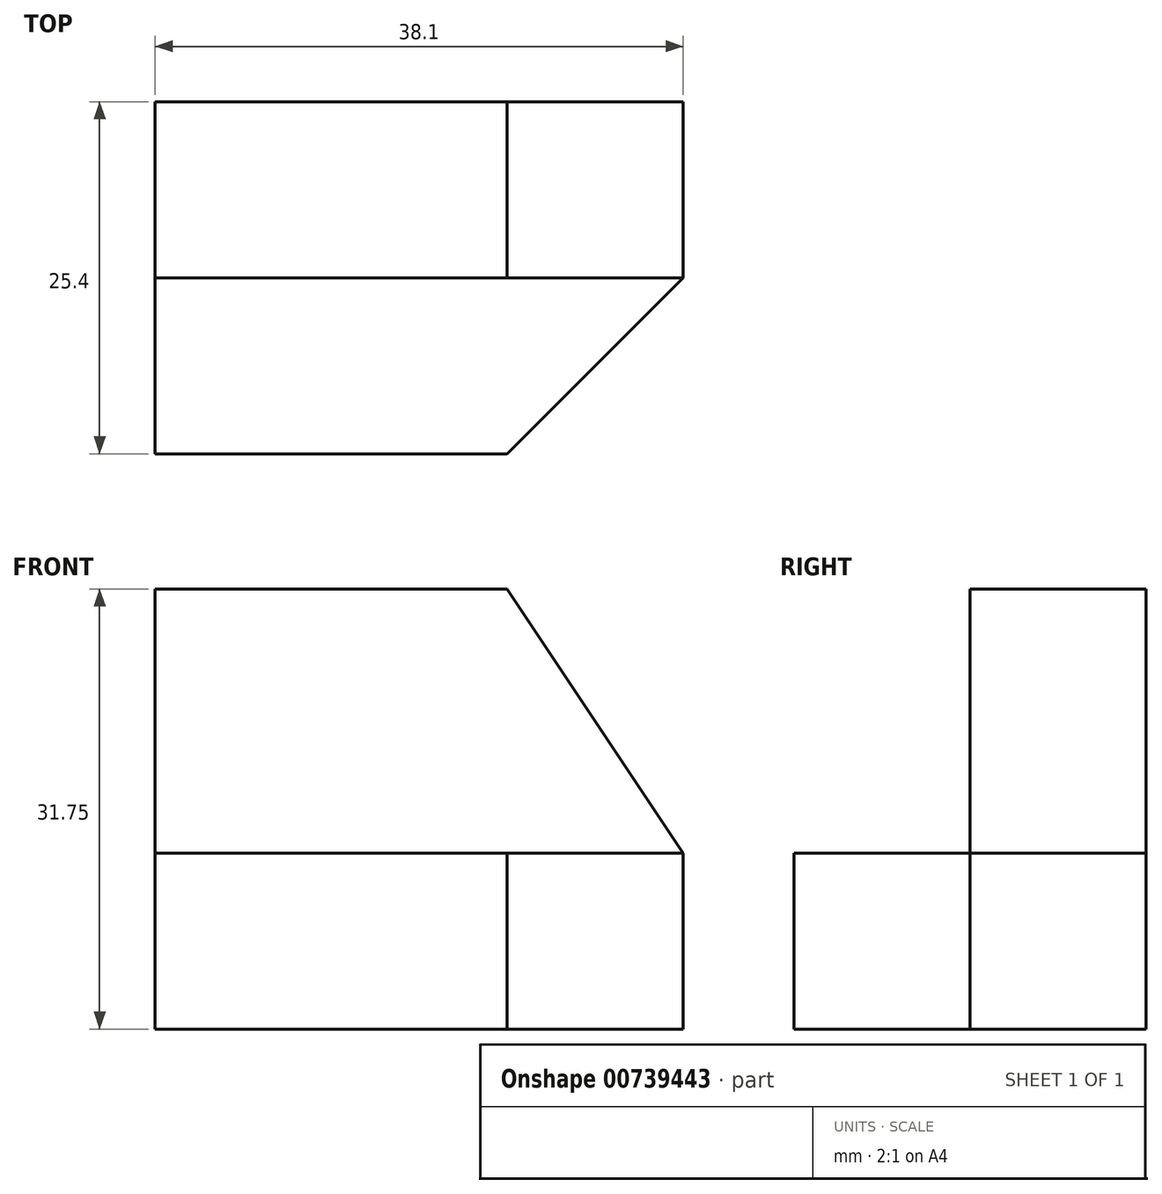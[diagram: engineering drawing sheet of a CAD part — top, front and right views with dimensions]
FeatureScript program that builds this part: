
annotation { "Feature Type Name" : "Feature", "Feature Type Description" : "" }
export const myFeature = defineFeature(function(context is Context, id is Id, definition is map)
    precondition{}
    {
        {
            var Q0;
            Q0=qCreatedBy(makeId("Front.planeOp"),FACE);
            var sketch = newSketch(context, id + "F0", { "sketchPlane" : qUnion([Q0])});
            skLineSegment(sketch, "E0.bottom", {"start": v(0, 0) * mm, "end": v(38.1, 0) * mm});
            skLineSegment(sketch, "E0.top", {"start": v(0, 31.75) * mm, "end": v(38.1, 31.75) * mm});
            skLineSegment(sketch, "E0.left", {"start": v(0, 0) * mm, "end": v(0, 31.75) * mm});
            skLineSegment(sketch, "E0.right", {"start": v(38.1, 0) * mm, "end": v(38.1, 31.75) * mm});
            skSolve(sketch);
        }
        {
            var Q0;
            Q0=makeQuery(id+"F0.imprint","IMPRINT",FACE,{"disambiguationData":[TD([[makeQuery(id+"F0.imprint","IMPRINT",EDGE,{"derivedFrom":sQuery(id+"F0.wireOp",EDGE,"E0.bottom")}),1.0]])]});
            extrude(context, id + "F1", {"entities" : qUnion([Q0]), "depth" : 25.4 * mm, "offsetDistance" : 25.4 * mm});
        }
        {
            var Q0;
            Q0=makeQuery(id+"F1.opExtrude","SWEPT_FACE",FACE,{"disambiguationData":[OSD([sQuery(id+"F0.wireOp",EDGE,"E0.right")])]});
            var sketch = newSketch(context, id + "F2", { "sketchPlane" : qUnion([Q0])});
            skLineSegment(sketch, "E1.bottom", {"start": v(-25.4, 31.75) * mm, "end": v(-12.7, 31.75) * mm});
            skLineSegment(sketch, "E1.top", {"start": v(-25.4, 12.7) * mm, "end": v(-12.7, 12.7) * mm});
            skLineSegment(sketch, "E1.left", {"start": v(-25.4, 31.75) * mm, "end": v(-25.4, 12.7) * mm});
            skLineSegment(sketch, "E1.right", {"start": v(-12.7, 31.75) * mm, "end": v(-12.7, 12.7) * mm});
            skSolve(sketch);
        }
        {
            var Q0;
            Q0=makeQuery(id+"F2.imprint","IMPRINT",FACE,{"disambiguationData":[TD([[makeQuery(id+"F2.imprint","IMPRINT",EDGE,{"derivedFrom":sQuery(id+"F2.wireOp",EDGE,"E1.bottom")}),-1.0]])]});
            extrude(context, id + "F3", {"entities" : qUnion([Q0]), "operationType" : NewBodyOperationType.REMOVE, "oppositeDirection" : true, "depth" : 38.1 * mm, "offsetDistance" : 25.4 * mm});
        }
        {
            var Q0;
            Q0=makeQuery(id+"F3.boolean.opBoolean","COPY",FACE,{"derivedFrom":makeQuery(id+"F3.opExtrude","SWEPT_FACE",FACE,{"disambiguationData":[OSD([sQuery(id+"F2.wireOp",EDGE,"E1.right")])]})});
            var sketch = newSketch(context, id + "F4", { "sketchPlane" : qUnion([Q0])});
            skLineSegment(sketch, "E2", {"start": v(25.4, 31.75) * mm, "end": v(38.1, 12.7) * mm});
            skLineSegment(sketch, "E3", {"start": v(38.1, 12.7) * mm, "end": v(38.1, 31.75) * mm});
            skLineSegment(sketch, "E4", {"start": v(38.1, 31.75) * mm, "end": v(25.4, 31.75) * mm});
            skSolve(sketch);
        }
        {
            var Q0;
            Q0=makeQuery(id+"F4.imprint","IMPRINT",FACE,{"disambiguationData":[TD([[makeQuery(id+"F4.imprint","IMPRINT",EDGE,{"derivedFrom":sQuery(id+"F4.wireOp",EDGE,"E2")}),1.0]])]});
            extrude(context, id + "F5", {"entities" : qUnion([Q0]), "operationType" : NewBodyOperationType.REMOVE, "oppositeDirection" : true, "depth" : 12.7 * mm, "offsetDistance" : 25.4 * mm});
        }
        {
            var Q0;
            Q0=makeQuery(id+"F3.boolean.opBoolean","COPY",FACE,{"derivedFrom":makeQuery(id+"F3.opExtrude","SWEPT_FACE",FACE,{"disambiguationData":[OSD([sQuery(id+"F2.wireOp",EDGE,"E1.top")])]})});
            var sketch = newSketch(context, id + "F6", { "sketchPlane" : qUnion([Q0])});
            skLineSegment(sketch, "E5", {"start": v(38.1, -12.7) * mm, "end": v(25.4, -25.4) * mm});
            skLineSegment(sketch, "E6", {"start": v(25.4, -25.4) * mm, "end": v(38.1, -25.4) * mm});
            skLineSegment(sketch, "E7", {"start": v(38.1, -25.4) * mm, "end": v(38.1, -12.7) * mm});
            skSolve(sketch);
        }
        {
            var Q0;
            Q0=makeQuery(id+"F6.imprint","IMPRINT",FACE,{"disambiguationData":[TD([[makeQuery(id+"F6.imprint","IMPRINT",EDGE,{"derivedFrom":sQuery(id+"F6.wireOp",EDGE,"E5")}),1.0]])]});
            extrude(context, id + "F7", {"entities" : qUnion([Q0]), "operationType" : NewBodyOperationType.REMOVE, "oppositeDirection" : true, "depth" : 12.7 * mm, "offsetDistance" : 25.4 * mm});
        }
    });
